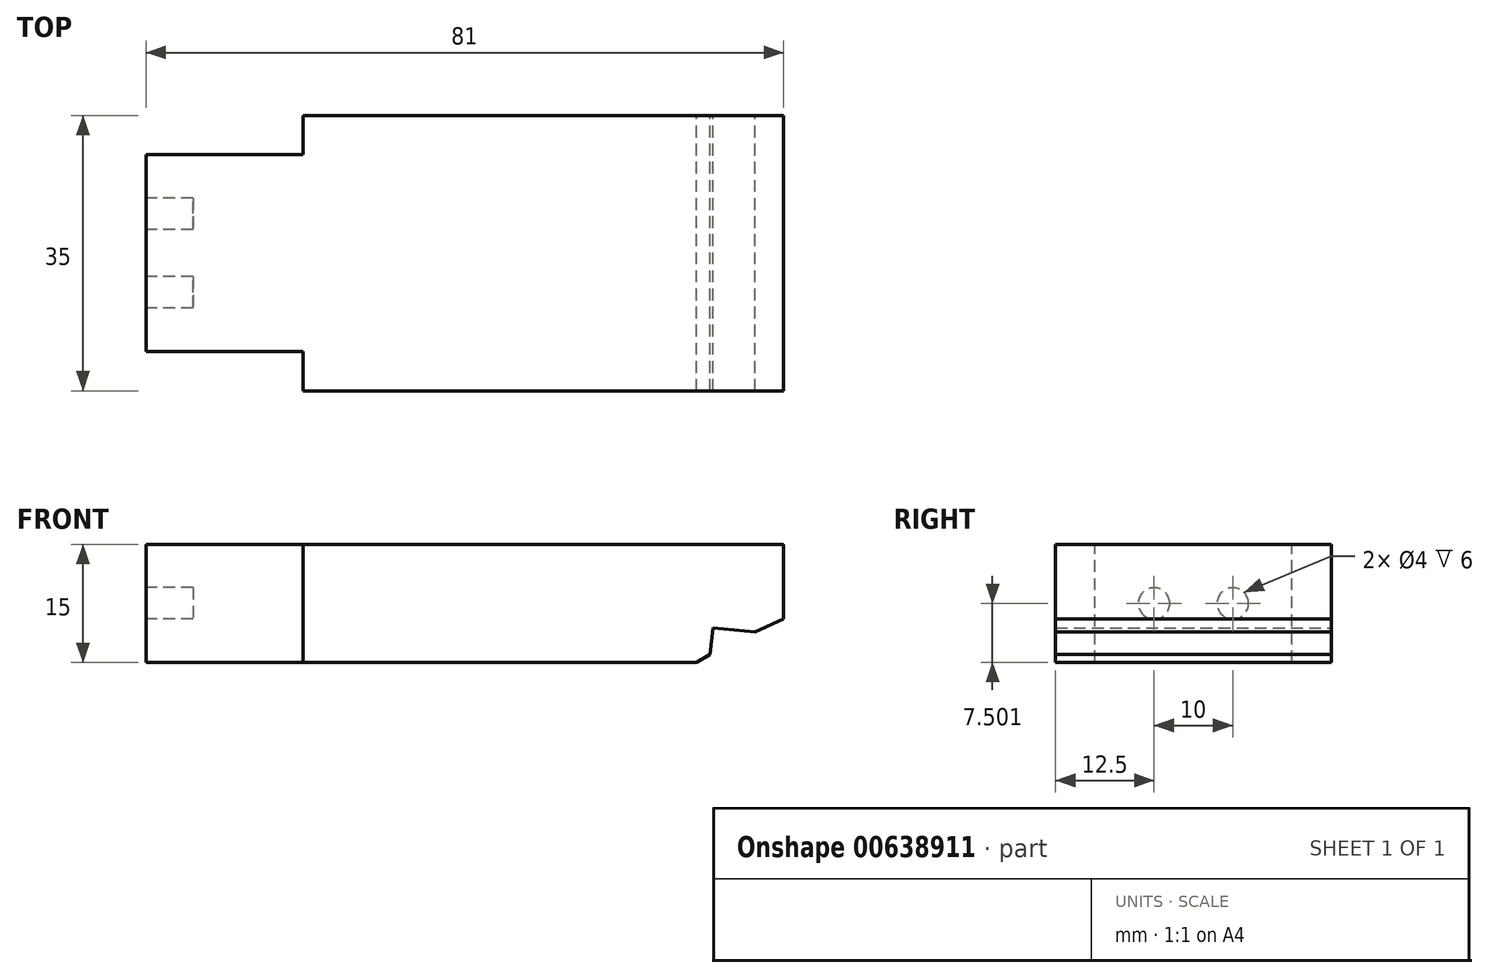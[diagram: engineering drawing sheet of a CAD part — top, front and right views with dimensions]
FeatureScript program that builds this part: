
annotation { "Feature Type Name" : "Feature", "Feature Type Description" : "" }
export const myFeature = defineFeature(function(context is Context, id is Id, definition is map)
    precondition{}
    {
        {
            var Q0;
            Q0=qCreatedBy(makeId("Front.planeOp"),FACE);
            var sketch = newSketch(context, id + "F0", { "sketchPlane" : qUnion([Q0])});
            skLineSegment(sketch, "E0", {"start": v(88.82, -34.23) * mm, "end": v(88.82, -49.23) * mm});
            skLineSegment(sketch, "E1", {"start": v(98.82, -34.23) * mm, "end": v(98.82, -49.23) * mm});
            skLineSegment(sketch, "E2", {"start": v(73.82, -34.23) * mm, "end": v(73.82, -49.23) * mm});
            skCircle(sketch, "E3", {"center": v(76.32, -41.73) * mm, "radius": 2 * mm});
            skCircle(sketch, "E4", {"center": v(86.32, -41.73) * mm, "radius": 2 * mm});
            skCircle(sketch, "E5", {"center": v(68.82, -41.73) * mm, "radius": 2.5 * mm});
            skCircle(sketch, "E6", {"center": v(93.82, -41.73) * mm, "radius": 2.5 * mm});
            skLineSegment(sketch, "E7", {"start": v(98.82, -49.23) * mm, "end": v(63.82, -49.23) * mm});
            skLineSegment(sketch, "E8", {"start": v(63.82, -34.23) * mm, "end": v(98.82, -34.23) * mm});
            skLineSegment(sketch, "E9", {"start": v(63.82, -34.23) * mm, "end": v(63.82, -49.23) * mm});
            skLineSegment(sketch, "E10", {"start": v(73.82, -48.23) * mm, "end": v(88.82, -48.23) * mm});
            skLineSegment(sketch, "E11", {"start": v(73.82, -45.37) * mm, "end": v(88.82, -45.37) * mm});
            skLineSegment(sketch, "E12", {"start": v(73.82, -43.72) * mm, "end": v(88.82, -43.72) * mm});
            skLineSegment(sketch, "E13", {"start": v(-96.82, -49.23) * mm, "end": v(-26.89, -49.23) * mm});
            skLineSegment(sketch, "E14", {"start": v(-15.82, -34.23) * mm, "end": v(-96.82, -34.23) * mm});
            skLineSegment(sketch, "E15", {"start": v(-15.82, -34.23) * mm, "end": v(-15.82, -43.72) * mm});
            skLineSegment(sketch, "E16", {"start": v(-19.47, -45.37) * mm, "end": v(-24.82, -44.84) * mm});
            skLineSegment(sketch, "E17", {"start": v(-15.82, -43.72) * mm, "end": v(-19.47, -45.37) * mm});
            skLineSegment(sketch, "E18", {"start": v(-25.15, -48.23) * mm, "end": v(-24.82, -44.84) * mm});
            skLineSegment(sketch, "E19", {"start": v(-25.15, -48.23) * mm, "end": v(-26.89, -49.23) * mm});
            skLineSegment(sketch, "E20", {"start": v(-74.82, -41.73) * mm, "end": v(-98.82, -41.73) * mm});
            skLineSegment(sketch, "E21", {"start": v(-96.82, -39.23) * mm, "end": v(-96.82, -49.23) * mm});
            skLineSegment(sketch, "E22", {"start": v(-96.82, -39.23) * mm, "end": v(-96.82, -34.23) * mm});
            skLineSegment(sketch, "E23", {"start": v(-76.82, -39.23) * mm, "end": v(-76.82, -34.23) * mm});
            skLineSegment(sketch, "E24", {"start": v(-76.82, -39.23) * mm, "end": v(-76.82, -49.23) * mm});
            skLineSegment(sketch, "E25", {"start": v(-15.82, 24.23) * mm, "end": v(-15.82, 39.23) * mm});
            skLineSegment(sketch, "E26", {"start": v(-76.82, 49.23) * mm, "end": v(-76.82, 39.23) * mm});
            skLineSegment(sketch, "E27", {"start": v(-96.82, 49.23) * mm, "end": v(-96.82, 14.23) * mm});
            skLineSegment(sketch, "E28", {"start": v(-76.82, 14.23) * mm, "end": v(-96.82, 14.23) * mm});
            skLineSegment(sketch, "E29", {"start": v(-76.82, 24.23) * mm, "end": v(-15.82, 24.23) * mm});
            skLineSegment(sketch, "E30", {"start": v(-76.82, 49.23) * mm, "end": v(-96.82, 49.23) * mm});
            skLineSegment(sketch, "E31", {"start": v(-76.82, 39.23) * mm, "end": v(-15.82, 39.23) * mm});
            skLineSegment(sketch, "E32", {"start": v(-76.82, 24.23) * mm, "end": v(-76.82, 14.23) * mm});
            skLineSegment(sketch, "E33", {"start": v(-74.82, 19.23) * mm, "end": v(-98.82, 19.23) * mm});
            skLineSegment(sketch, "E34", {"start": v(-74.82, 44.23) * mm, "end": v(-98.82, 44.23) * mm});
            skLineSegment(sketch, "E35", {"start": v(-24.82, 39.23) * mm, "end": v(-24.82, 24.23) * mm});
            skSolve(sketch);
        }
        {
            var Q0;
            {var subQ0=sQuery(id+"F0.wireOp",EDGE,"E21");var subQ1=sQuery(id+"F0.wireOp",EDGE,"E13");var subQ2=makeQuery(id+"F0.imprint","INTERSECT",VERTEX,{"derivedFrom":[subQ1,subQ0]});Q0=makeQuery(id+"F0.imprint","IMPRINT",FACE,{"disambiguationData":[TD([[makeQuery(id+"F0.imprint","IMPRINT",EDGE,{"disambiguationData":[TD([[subQ2,-1.0]])],"derivedFrom":subQ1}),1.0]])]});}
            var Q1;
            {var subQ0=sQuery(id+"F0.wireOp",EDGE,"E15");Q1=makeQuery(id+"F0.imprint","IMPRINT",FACE,{"disambiguationData":[TD([[makeQuery(id+"F0.imprint","IMPRINT",EDGE,{"derivedFrom":subQ0}),-1.0]])]});}
            var Q2;
            {var subQ0=sQuery(id+"F0.wireOp",EDGE,"E22");Q2=makeQuery(id+"F0.imprint","IMPRINT",FACE,{"disambiguationData":[TD([[makeQuery(id+"F0.imprint","IMPRINT",EDGE,{"derivedFrom":subQ0}),-1.0]])]});}
            extrude(context, id + "F1", {"entities" : qUnion([Q0, Q1, Q2]), "depth" : 35 * mm, "offsetDistance" : 25 * mm});
        }
        {
            var Q0;
            Q0=makeQuery(id+"F1.opExtrude","SWEPT_FACE",FACE,{"disambiguationData":[OSD([sQuery(id+"F0.wireOp",EDGE,"E14")])]});
            var sketch = newSketch(context, id + "F2", { "sketchPlane" : qUnion([Q0])});
            skLineSegment(sketch, "E36.0", {"start": v(-96.82, -35) * mm, "end": v(-96.82, 0) * mm});
            skLineSegment(sketch, "E37.0", {"start": v(-15.82, 0) * mm, "end": v(-96.82, 0) * mm});
            skLineSegment(sketch, "E38.0", {"start": v(-15.82, -35) * mm, "end": v(-15.82, 0) * mm});
            skLineSegment(sketch, "E39.0", {"start": v(-15.82, -35) * mm, "end": v(-96.82, -35) * mm});
            skLineSegment(sketch, "E40", {"start": v(-15.82, -25) * mm, "end": v(-15.82, -10) * mm});
            skLineSegment(sketch, "E41", {"start": v(-76.82, 0) * mm, "end": v(-76.82, -10) * mm});
            skLineSegment(sketch, "E42", {"start": v(-96.82, 0) * mm, "end": v(-96.82, -35) * mm});
            skLineSegment(sketch, "E43", {"start": v(-76.82, -35) * mm, "end": v(-96.82, -35) * mm});
            skLineSegment(sketch, "E44", {"start": v(-76.82, -25) * mm, "end": v(-15.82, -25) * mm});
            skLineSegment(sketch, "E45", {"start": v(-76.82, 0) * mm, "end": v(-96.82, 0) * mm});
            skLineSegment(sketch, "E46", {"start": v(-76.82, -10) * mm, "end": v(-15.82, -10) * mm});
            skLineSegment(sketch, "E47", {"start": v(-76.82, -25) * mm, "end": v(-76.82, -35) * mm});
            skLineSegment(sketch, "E48", {"start": v(-74.82, -30) * mm, "end": v(-98.82, -30) * mm});
            skLineSegment(sketch, "E49", {"start": v(-74.82, -5) * mm, "end": v(-98.82, -5) * mm});
            skLineSegment(sketch, "E50", {"start": v(-24.82, -10) * mm, "end": v(-24.82, -25) * mm});
            skSolve(sketch);
        }
        {
            var Q0;
            {var subQ4=sQuery(id+"F2.wireOp",EDGE,"E39.0");Q0=makeQuery(id+"F2.imprint","IMPRINT",FACE,{"disambiguationData":[TD([[makeQuery(id+"F2.imprint","IMPRINT",EDGE,{"derivedFrom":subQ4}),-1.0]])]});}
            var Q1;
            {var subQ5=sQuery(id+"F2.wireOp",EDGE,"E37.0");Q1=makeQuery(id+"F2.imprint","IMPRINT",FACE,{"disambiguationData":[TD([[makeQuery(id+"F2.imprint","IMPRINT",EDGE,{"derivedFrom":subQ5}),1.0]])]});}
            extrude(context, id + "F3", {"entities" : qUnion([Q0, Q1]), "operationType" : NewBodyOperationType.REMOVE, "endBound" : BoundingType.THROUGH_ALL, "oppositeDirection" : true, "depth" : 25 * mm, "offsetDistance" : 25 * mm});
        }
        {
            var Q0;
            Q0=makeQuery(id+"F3.boolean.opBoolean","COPY",FACE,{"derivedFrom":makeQuery(id+"F3.opExtrude","SWEPT_FACE",FACE,{"disambiguationData":[OSD([sQuery(id+"F2.wireOp",EDGE,"E47")])]})});
            var sketch = newSketch(context, id + "F4", { "sketchPlane" : qUnion([Q0])});
            skLineSegment(sketch, "E51.0", {"start": v(-35, -49.23) * mm, "end": v(-35, -34.23) * mm});
            skLineSegment(sketch, "E52.0", {"start": v(-25, -34.23) * mm, "end": v(-35, -34.23) * mm});
            skLineSegment(sketch, "E53.0", {"start": v(-25, -49.23) * mm, "end": v(-35, -49.23) * mm});
            skLineSegment(sketch, "E54", {"start": v(-10, -34.23) * mm, "end": v(-10, -49.23) * mm});
            skLineSegment(sketch, "E55", {"start": v(0, -34.23) * mm, "end": v(0, -49.23) * mm});
            skLineSegment(sketch, "E56", {"start": v(-25, -34.23) * mm, "end": v(-25, -49.23) * mm});
            skCircle(sketch, "E57", {"center": v(-22.5, -41.73) * mm, "radius": 2 * mm});
            skCircle(sketch, "E58", {"center": v(-12.5, -41.73) * mm, "radius": 2 * mm});
            skCircle(sketch, "E59", {"center": v(-30, -41.73) * mm, "radius": 2.5 * mm});
            skCircle(sketch, "E60", {"center": v(-5, -41.73) * mm, "radius": 2.5 * mm});
            skLineSegment(sketch, "E61", {"start": v(0, -49.23) * mm, "end": v(-35, -49.23) * mm});
            skLineSegment(sketch, "E62", {"start": v(-35, -34.23) * mm, "end": v(0, -34.23) * mm});
            skLineSegment(sketch, "E63", {"start": v(-35, -34.23) * mm, "end": v(-35, -49.23) * mm});
            skLineSegment(sketch, "E64", {"start": v(-25, -48.23) * mm, "end": v(-10, -48.23) * mm});
            skLineSegment(sketch, "E65", {"start": v(-25, -45.37) * mm, "end": v(-10, -45.37) * mm});
            skLineSegment(sketch, "E66", {"start": v(-25, -43.72) * mm, "end": v(-10, -43.72) * mm});
            skSolve(sketch);
        }
        {
            var Q0;
            Q0=makeQuery(id+"F1.opExtrude","SWEPT_FACE",FACE,{"disambiguationData":[OSD([sQuery(id+"F0.wireOp",EDGE,"E21"),sQuery(id+"F0.wireOp",EDGE,"E22")])]});
            var sketch = newSketch(context, id + "F5", { "sketchPlane" : qUnion([Q0])});
            skCircle(sketch, "E67.0", {"center": v(22.5, -41.73) * mm, "radius": 2 * mm});
            skCircle(sketch, "E68.0", {"center": v(12.5, -41.73) * mm, "radius": 2 * mm});
            skSolve(sketch);
        }
        {
            var Q0;
            Q0=makeQuery(id+"F4.imprint","IMPRINT",FACE,{"disambiguationData":[TD([[makeQuery(id+"F4.imprint","IMPRINT",EDGE,{"derivedFrom":sQuery(id+"F4.wireOp",EDGE,"E60")}),-1.0]])]});
            var Q1;
            Q1=makeQuery(id+"F4.imprint","IMPRINT",FACE,{"disambiguationData":[TD([[makeQuery(id+"F4.imprint","IMPRINT",EDGE,{"derivedFrom":sQuery(id+"F4.wireOp",EDGE,"E59")}),-1.0]])]});
            extrude(context, id + "F6", {"entities" : qUnion([Q0, Q1]), "operationType" : NewBodyOperationType.REMOVE, "endBound" : BoundingType.THROUGH_ALL, "oppositeDirection" : true, "depth" : 25 * mm, "offsetDistance" : 25 * mm});
        }
        {
            var Q0;
            Q0=makeQuery(id+"F5.imprint","IMPRINT",FACE,{"disambiguationData":[TD([[makeQuery(id+"F5.imprint","IMPRINT",EDGE,{"derivedFrom":sQuery(id+"F5.wireOp",EDGE,"E67.0")}),1.0]])]});
            var Q1;
            Q1=makeQuery(id+"F5.imprint","IMPRINT",FACE,{"disambiguationData":[TD([[makeQuery(id+"F5.imprint","IMPRINT",EDGE,{"derivedFrom":sQuery(id+"F5.wireOp",EDGE,"E68.0")}),1.0]])]});
            extrude(context, id + "F7", {"entities" : qUnion([Q0, Q1]), "operationType" : NewBodyOperationType.REMOVE, "oppositeDirection" : true, "depth" : 6 * mm, "offsetDistance" : 25 * mm});
        }
    });
